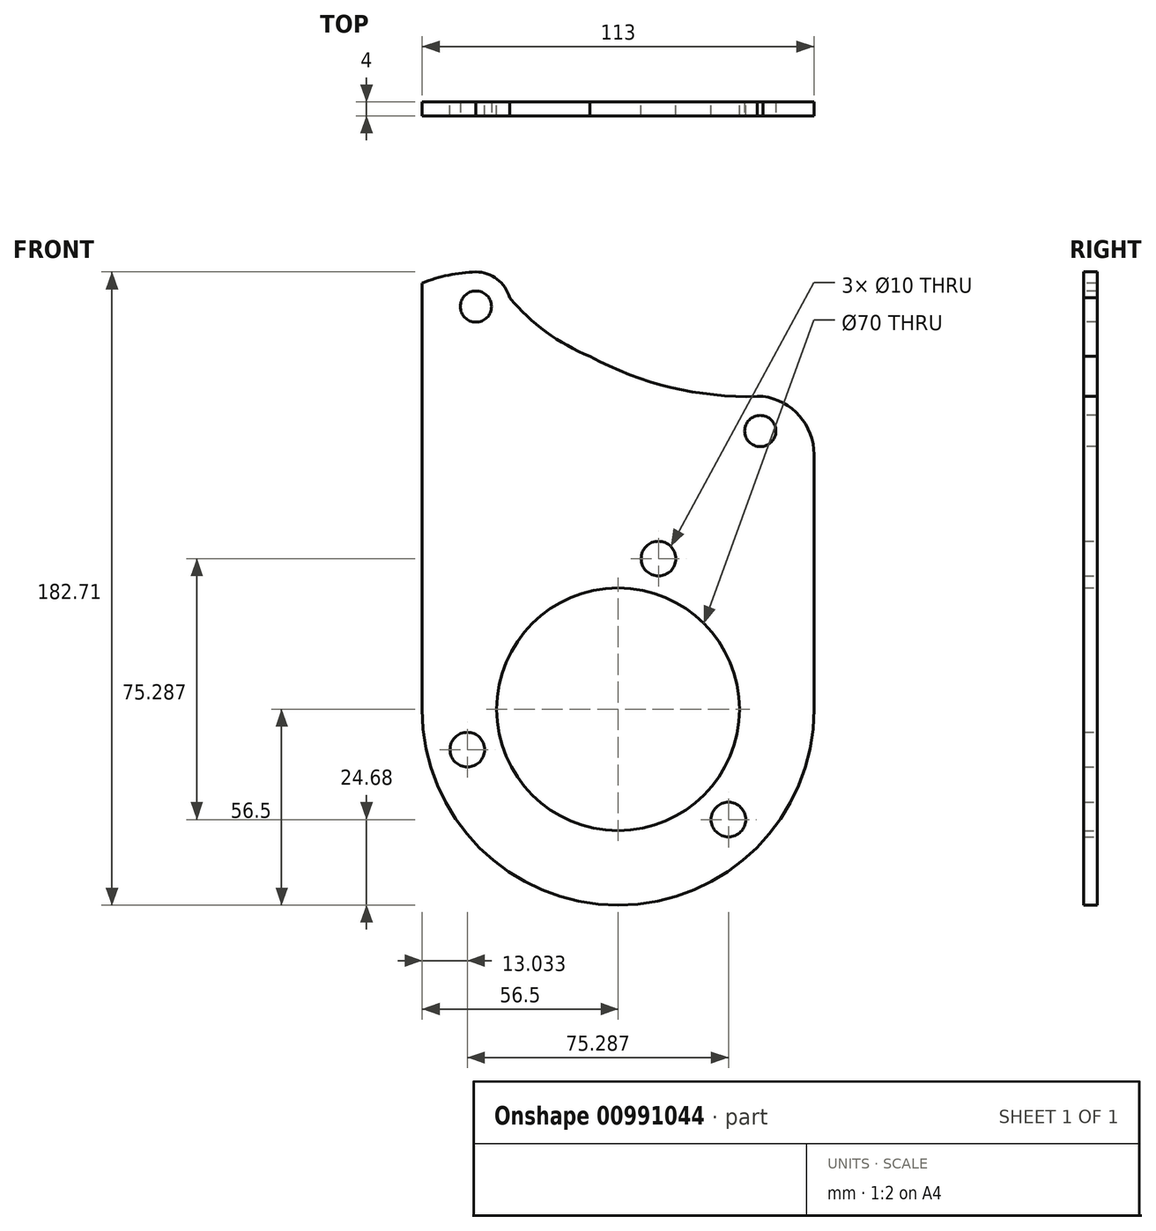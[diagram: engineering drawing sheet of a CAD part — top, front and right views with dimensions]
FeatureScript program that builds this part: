
annotation { "Feature Type Name" : "Feature", "Feature Type Description" : "" }
export const myFeature = defineFeature(function(context is Context, id is Id, definition is map)
    precondition{}
    {
        {
            var Q0;
            Q0=qCreatedBy(makeId("Front.planeOp"),FACE);
            var sketch = newSketch(context, id + "F0", { "sketchPlane" : qUnion([Q0])});
            skCircle(sketch, "E0", {"center": v(0, 0) * mm, "radius": 56.5 * mm});
            skCircle(sketch, "E1", {"center": v(0, 0) * mm, "radius": 35 * mm});
            skCircle(sketch, "E2", {"center": v(0, 0) * mm, "radius": 45 * mm, "construction": true});
            skCircle(sketch, "E3", {"center": v(0, 45) * mm, "radius": 5 * mm});
            skCircle(sketch, "E4.1.0", {"center": v(-38.97, -22.5) * mm, "radius": 5 * mm});
            skCircle(sketch, "E4.2.0", {"center": v(38.97, -22.5) * mm, "radius": 5 * mm});
            skSolve(sketch);
        }
        {
            var Q0;
            Q0 = qSketchRegion(id + "F0", true);
            extrude(context, id + "F1", {"entities" : qUnion([Q0]), "depth" : 4 * mm, "offsetDistance" : 25 * mm});
        }
        {
            var Q0;
            Q0=makeQuery(id+"F1.opExtrude","SWEPT_BODY",BODY,{"disambiguationData":[OSD([sQuery(id+"F0.wireOp",EDGE,"E0"),sQuery(id+"F0.wireOp",EDGE,"E1"),sQuery(id+"F0.wireOp",EDGE,"E3"),sQuery(id+"F0.wireOp",EDGE,"E4.1.0"),sQuery(id+"F0.wireOp",EDGE,"E4.2.0")])]});
            var Q1;
            Q1=makeQuery(id+"F1.opExtrude","CAP_EDGE",EDGE,{"disambiguationData":[OSD([sQuery(id+"F0.wireOp",EDGE,"E1")])],"isStart":false});
            transform(context, id + "F2", {"entities" : qUnion([Q0]), "transformType" : TransformType.ROTATION, "transformAxis" : qUnion([Q1]), "angle" : 15 * degree, "oppositeDirection" : true, "makeCopy" : false});
        }
        {
            var Q0;
            Q0=makeQuery(id+"F1.opExtrude","CAP_FACE",FACE,{"disambiguationData":[OSD([sQuery(id+"F0.wireOp",EDGE,"E0"),sQuery(id+"F0.wireOp",EDGE,"E1"),sQuery(id+"F0.wireOp",EDGE,"E3"),sQuery(id+"F0.wireOp",EDGE,"E4.1.0"),sQuery(id+"F0.wireOp",EDGE,"E4.2.0")])],"isStart":false});
            var sketch = newSketch(context, id + "F3", { "sketchPlane" : qUnion([Q0])});
            skLineSegment(sketch, "E5", {"start": v(-56.5, 0) * mm, "end": v(-56.5, 123) * mm});
            skLineSegment(sketch, "E6", {"start": v(56.5, 0) * mm, "end": v(56.5, 73.5) * mm});
            skLineSegment(sketch, "E7", {"start": v(56.5, 73.5) * mm, "end": v(-56.5, 123) * mm, "construction": true});
            skLineSegment(sketch, "E8", {"start": v(-56.5, 123) * mm, "end": v(-40.99, 116.2) * mm, "construction": true});
            skLineSegment(sketch, "E9", {"start": v(56.5, 73.5) * mm, "end": v(40.99, 80.3) * mm, "construction": true});
            skCircle(sketch, "E10", {"center": v(40.99, 80.3) * mm, "radius": 4.5 * mm});
            skCircle(sketch, "E11", {"center": v(-40.99, 116.2) * mm, "radius": 4.5 * mm});
            skCircle(sketch, "E12", {"center": v(-40.99, 116.2) * mm, "radius": 10 * mm});
            skCircle(sketch, "E13", {"center": v(40.99, 80.3) * mm, "radius": 10 * mm});
            skArc(sketch, "E14", {"start": v(-40.99, 126.2) * mm, "mid": v(-48.88, 125.26) * mm, "end": v(-56.5, 123) * mm});
            skArc(sketch, "E15", {"start": v(-31.3, 118.71) * mm, "mid": v(-20.74, 108.9) * mm, "end": v(-8.16, 101.82) * mm});
            skArc(sketch, "E16", {"start": v(-8.16, 101.82) * mm, "mid": v(15.24, 92.86) * mm, "end": v(40.17, 90.26) * mm});
            skArc(sketch, "E17", {"start": v(56.5, 73.5) * mm, "mid": v(52.3, 84.64) * mm, "end": v(41.8, 90.26) * mm});
            skSolve(sketch);
        }
        {
            var Q0;
            {var subQ9=sQuery(id+"F3.wireOp",EDGE,"E5");Q0=makeQuery(id+"F3.imprint","IMPRINT",FACE,{"disambiguationData":[TD([[makeQuery(id+"F3.imprint","IMPRINT",EDGE,{"derivedFrom":subQ9}),-1.0]])]});}
            var Q1;
            Q1=makeQuery(id+"F3.imprint","IMPRINT",FACE,{"disambiguationData":[TD([[makeQuery(id+"F3.imprint","IMPRINT",EDGE,{"derivedFrom":sQuery(id+"F3.wireOp",EDGE,"E11")}),-1.0]])]});
            var Q2;
            Q2=makeQuery(id+"F3.imprint","IMPRINT",FACE,{"disambiguationData":[TD([[makeQuery(id+"F3.imprint","IMPRINT",EDGE,{"derivedFrom":sQuery(id+"F3.wireOp",EDGE,"E10")}),-1.0]])]});
            extrude(context, id + "F4", {"entities" : qUnion([Q0, Q1, Q2]), "operationType" : NewBodyOperationType.ADD, "oppositeDirection" : true, "depth" : 4 * mm, "offsetDistance" : 25 * mm});
        }
    });
